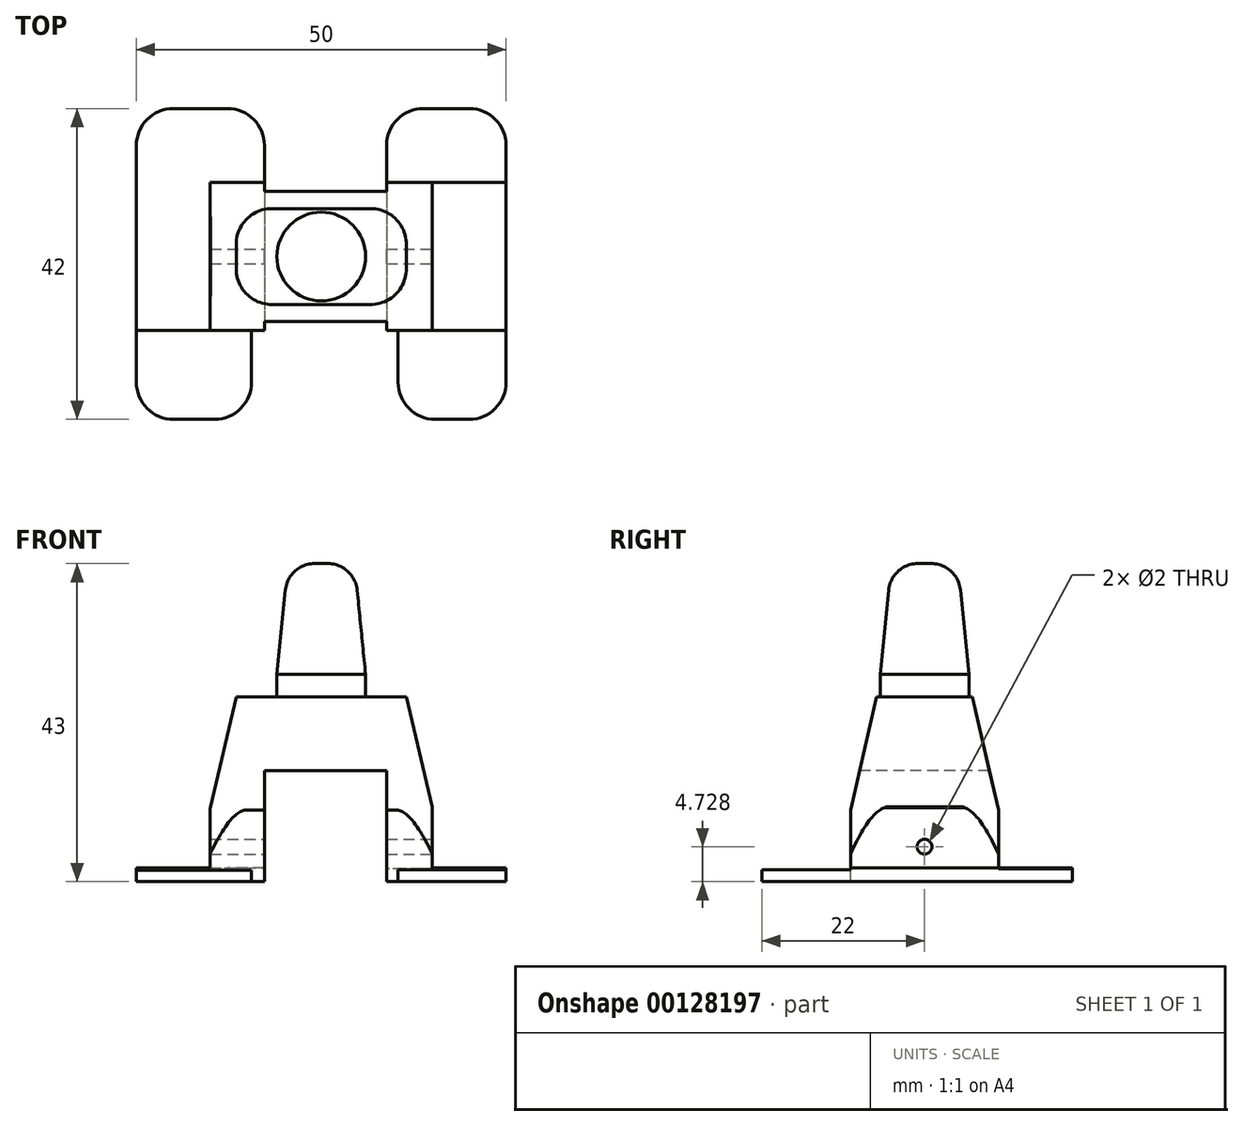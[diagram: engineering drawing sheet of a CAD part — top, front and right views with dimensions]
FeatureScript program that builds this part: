
annotation { "Feature Type Name" : "Feature", "Feature Type Description" : "" }
export const myFeature = defineFeature(function(context is Context, id is Id, definition is map)
    precondition{}
    {
        {
            var Q0;
            Q0=qCreatedBy(makeId("Front.planeOp"),FACE);
            var sketch = newSketch(context, id + "F0", { "sketchPlane" : qUnion([Q0])});
            skLineSegment(sketch, "E0.bottom", {"start": v(15, -12.5) * mm, "end": v(-15, -12.5) * mm});
            skLineSegment(sketch, "E0.top", {"start": v(15, 12.5) * mm, "end": v(-15, 12.5) * mm});
            skLineSegment(sketch, "E0.left", {"start": v(15, -12.5) * mm, "end": v(15, 12.5) * mm});
            skLineSegment(sketch, "E0.right", {"start": v(-15, -12.5) * mm, "end": v(-15, 12.5) * mm});
            skPoint(sketch, "E0.middle", {"position": v(0, 0) * mm});
            skSolve(sketch);
        }
        {
            var Q0;
            Q0=makeQuery(id+"F0.imprint","IMPRINT",FACE,{"disambiguationData":[TD([[makeQuery(id+"F0.imprint","IMPRINT",EDGE,{"derivedFrom":sQuery(id+"F0.wireOp",EDGE,"E0.bottom")}),-1.0]])]});
            extrude(context, id + "F1", {"entities" : qUnion([Q0]), "depth" : 20 * mm});
        }
        {
            var Q0;
            Q0=makeQuery(id+"F1.opExtrude","CAP_FACE",FACE,{"disambiguationData":[OSD([sQuery(id+"F0.wireOp",EDGE,"E0.bottom"),sQuery(id+"F0.wireOp",EDGE,"E0.top"),sQuery(id+"F0.wireOp",EDGE,"E0.left"),sQuery(id+"F0.wireOp",EDGE,"E0.right")])],"isStart":false});
            var sketch = newSketch(context, id + "F2", { "sketchPlane" : qUnion([Q0])});
            skLineSegment(sketch, "E1.bottom", {"start": v(-7.68, -12.5) * mm, "end": v(8.82, -12.5) * mm});
            skLineSegment(sketch, "E1.top", {"start": v(-7.68, 2.5) * mm, "end": v(8.82, 2.5) * mm});
            skLineSegment(sketch, "E1.left", {"start": v(-7.68, -12.5) * mm, "end": v(-7.68, 2.5) * mm});
            skLineSegment(sketch, "E1.right", {"start": v(8.82, -12.5) * mm, "end": v(8.82, 2.5) * mm});
            skSolve(sketch);
        }
        {
            var Q0;
            Q0=makeQuery(id+"F2.imprint","IMPRINT",FACE,{"disambiguationData":[TD([[makeQuery(id+"F2.imprint","IMPRINT",EDGE,{"derivedFrom":sQuery(id+"F2.wireOp",EDGE,"E1.bottom")}),-1.0]])]});
            extrude(context, id + "F3", {"entities" : qUnion([Q0]), "operationType" : NewBodyOperationType.REMOVE, "endBound" : BoundingType.THROUGH_ALL, "oppositeDirection" : true, "depth" : 25 * mm});
        }
        {
            var Q0;
            Q0=makeQuery(id+"F1.opExtrude","SWEPT_EDGE",EDGE,{"disambiguationData":[OSD([sQuery(id+"F0.wireOp",EDGE,"E0.top"),sQuery(id+"F0.wireOp",EDGE,"E0.left")])]});
            chamfer(context, id + "F4", {"entities" : qUnion([Q0]), "chamferType" : ChamferType.TWO_OFFSETS, "width1" : 2 * mm, "oppositeDirection" : false, "width2" : 15 * mm, "tangentPropagation" : true});
        }
        {
            var Q0;
            Q0=makeQuery(id+"F1.opExtrude","SWEPT_EDGE",EDGE,{"disambiguationData":[OSD([sQuery(id+"F0.wireOp",EDGE,"E0.top"),sQuery(id+"F0.wireOp",EDGE,"E0.right")])]});
            chamfer(context, id + "F5", {"entities" : qUnion([Q0]), "chamferType" : ChamferType.TWO_OFFSETS, "width1" : 15 * mm, "oppositeDirection" : false, "width2" : 2 * mm, "tangentPropagation" : true});
        }
        {
            var Q0;
            Q0=makeQuery(id+"F1.opExtrude","SWEPT_FACE",FACE,{"disambiguationData":[OSD([sQuery(id+"F0.wireOp",EDGE,"E0.top")])]});
            chamfer(context, id + "F6", {"entities" : qUnion([Q0]), "chamferType" : ChamferType.TWO_OFFSETS, "width1" : 1.5 * mm, "oppositeDirection" : false, "width2" : 15 * mm, "tangentPropagation" : true});
        }
        {
            var Q0;
            Q0=makeQuery(id+"F1.opExtrude","SWEPT_FACE",FACE,{"disambiguationData":[OSD([sQuery(id+"F0.wireOp",EDGE,"E0.top")])]});
            var sketch = newSketch(context, id + "F7", { "sketchPlane" : qUnion([Q0])});
            skCircle(sketch, "E2", {"center": v(0, -10) * mm, "radius": 6 * mm});
            skPoint(sketch, "E2.centerSnap0", {"position": v(-11.5, -10) * mm});
            skSolve(sketch);
        }
        {
            var Q0;
            {var subQ0=sQuery(id+"F7.wireOp",EDGE,"E2");var subQ1=sQuery(id+"F0.wireOp",EDGE,"E0.top");var subQ2=makeQuery(id+"F1.opExtrude","SWEPT_FACE",FACE,{"disambiguationData":[OSD([subQ1])]});var subQ3=makeQuery(id+"F6.opChamfer","BLEND_EDGE",EDGE,{"blendedFrom":[makeQuery(id+"F1.opExtrude","CAP_EDGE",EDGE,{"disambiguationData":[OSD([subQ1])],"isStart":true}),subQ2],"blendedInto":[subQ2]});var subQ4=makeQuery(id+"F7.imprint","INTERSECT",VERTEX,{"disambiguationData":[OD(0.0)],"derivedFrom":[subQ3,subQ0]});Q0=makeQuery(id+"F7.imprint","IMPRINT",FACE,{"disambiguationData":[TD([[makeQuery(id+"F7.imprint","IMPRINT",EDGE,{"disambiguationData":[TD([[subQ4,-1.0]])],"derivedFrom":subQ0}),1.0]])]});}
            extrude(context, id + "F8", {"entities" : qUnion([Q0]), "operationType" : NewBodyOperationType.ADD, "depth" : 18 * mm});
        }
        {
            var Q0;
            {var subQ0=sQuery(id+"F0.wireOp",EDGE,"E0.top");Q0=makeQuery(id+"F6.opChamfer","BLEND_EDGE",EDGE,{"blendedFrom":[makeQuery(id+"F4.opChamfer","BLEND_EDGE",EDGE,{"blendedFrom":[makeQuery(id+"F1.opExtrude","SWEPT_EDGE",EDGE,{"disambiguationData":[OSD([subQ0,sQuery(id+"F0.wireOp",EDGE,"E0.left")])]}),makeQuery(id+"F1.opExtrude","SWEPT_FACE",FACE,{"disambiguationData":[OSD([subQ0])]})],"blendedInto":[makeQuery(id+"F1.opExtrude","SWEPT_FACE",FACE,{"disambiguationData":[OSD([subQ0])]})]}),makeQuery(id+"F1.opExtrude","CAP_EDGE",EDGE,{"disambiguationData":[OSD([subQ0])],"isStart":false})],"blendedInto":[]});}
            var Q1;
            {var subQ0=sQuery(id+"F0.wireOp",EDGE,"E0.top");Q1=makeQuery(id+"F6.opChamfer","BLEND_EDGE",EDGE,{"blendedFrom":[makeQuery(id+"F4.opChamfer","BLEND_EDGE",EDGE,{"blendedFrom":[makeQuery(id+"F1.opExtrude","SWEPT_EDGE",EDGE,{"disambiguationData":[OSD([subQ0,sQuery(id+"F0.wireOp",EDGE,"E0.left")])]}),makeQuery(id+"F1.opExtrude","SWEPT_FACE",FACE,{"disambiguationData":[OSD([subQ0])]})],"blendedInto":[makeQuery(id+"F1.opExtrude","SWEPT_FACE",FACE,{"disambiguationData":[OSD([subQ0])]})]}),makeQuery(id+"F1.opExtrude","CAP_EDGE",EDGE,{"disambiguationData":[OSD([subQ0])],"isStart":true})],"blendedInto":[]});}
            var Q2;
            {var subQ0=sQuery(id+"F0.wireOp",EDGE,"E0.top");Q2=makeQuery(id+"F6.opChamfer","BLEND_EDGE",EDGE,{"blendedFrom":[makeQuery(id+"F5.opChamfer","BLEND_EDGE",EDGE,{"blendedFrom":[makeQuery(id+"F1.opExtrude","SWEPT_EDGE",EDGE,{"disambiguationData":[OSD([subQ0,sQuery(id+"F0.wireOp",EDGE,"E0.right")])]}),makeQuery(id+"F1.opExtrude","SWEPT_FACE",FACE,{"disambiguationData":[OSD([subQ0])]})],"blendedInto":[makeQuery(id+"F1.opExtrude","SWEPT_FACE",FACE,{"disambiguationData":[OSD([subQ0])]})]}),makeQuery(id+"F1.opExtrude","CAP_EDGE",EDGE,{"disambiguationData":[OSD([subQ0])],"isStart":false})],"blendedInto":[]});}
            var Q3;
            {var subQ0=sQuery(id+"F0.wireOp",EDGE,"E0.top");Q3=makeQuery(id+"F6.opChamfer","BLEND_EDGE",EDGE,{"blendedFrom":[makeQuery(id+"F5.opChamfer","BLEND_EDGE",EDGE,{"blendedFrom":[makeQuery(id+"F1.opExtrude","SWEPT_EDGE",EDGE,{"disambiguationData":[OSD([subQ0,sQuery(id+"F0.wireOp",EDGE,"E0.right")])]}),makeQuery(id+"F1.opExtrude","SWEPT_FACE",FACE,{"disambiguationData":[OSD([subQ0])]})],"blendedInto":[makeQuery(id+"F1.opExtrude","SWEPT_FACE",FACE,{"disambiguationData":[OSD([subQ0])]})]}),makeQuery(id+"F1.opExtrude","CAP_EDGE",EDGE,{"disambiguationData":[OSD([subQ0])],"isStart":true})],"blendedInto":[]});}
            fillet(context, id + "F9", {"entities" : qUnion([Q0, Q1, Q2, Q3]), "radius" : 5 * mm, "tangentPropagation" : true, "allowEdgeOverflow" : false});
        }
        {
            var Q0;
            Q0=makeQuery(id+"F1.opExtrude","SWEPT_FACE",FACE,{"disambiguationData":[OSD([sQuery(id+"F0.wireOp",EDGE,"E0.left")])]});
            var sketch = newSketch(context, id + "F10", { "sketchPlane" : qUnion([Q0])});
            skPoint(sketch, "E3", {"position": v(-10, -7.77) * mm});
            skPoint(sketch, "E3.positionSnap0", {"position": v(-10, -12.5) * mm});
            skSolve(sketch);
        }
        {
            var Q0;
            Q0=sQuery(id+"F10.wireOp",VERTEX,"E3");
            var Q1;
            Q1=makeQuery(id+"F1.opExtrude","SWEPT_BODY",BODY,{"disambiguationData":[OSD([sQuery(id+"F0.wireOp",EDGE,"E0.bottom"),sQuery(id+"F0.wireOp",EDGE,"E0.top"),sQuery(id+"F0.wireOp",EDGE,"E0.left"),sQuery(id+"F0.wireOp",EDGE,"E0.right")])]});
            hole(context, id + "F11", {"style" : HoleStyle.SIMPLE, "endStyle" : HoleEndStyle.THROUGH, "holeDiameter" : 2 * mm, "locations" : qUnion([Q0]), "scope" : qUnion([Q1]), "isTappedThrough" : true});
        }
        {
            var Q0;
            Q0=makeQuery(id+"F1.opExtrude","SWEPT_FACE",FACE,{"disambiguationData":[OSD([sQuery(id+"F0.wireOp",EDGE,"E0.left")])]});
            var sketch = newSketch(context, id + "F12", { "sketchPlane" : qUnion([Q0])});
            skLineSegment(sketch, "E4.bottom", {"start": v(-20, -12.5) * mm, "end": v(0, -12.5) * mm});
            skLineSegment(sketch, "E4.top", {"start": v(-20, -10.62) * mm, "end": v(0, -10.62) * mm});
            skLineSegment(sketch, "E4.left", {"start": v(-20, -12.5) * mm, "end": v(-20, -10.62) * mm});
            skLineSegment(sketch, "E4.right", {"start": v(0, -12.5) * mm, "end": v(0, -10.62) * mm});
            skSolve(sketch);
        }
        {
            var Q0;
            Q0=makeQuery(id+"F1.opExtrude","SWEPT_FACE",FACE,{"disambiguationData":[OSD([sQuery(id+"F0.wireOp",EDGE,"E0.right")])]});
            var sketch = newSketch(context, id + "F13", { "sketchPlane" : qUnion([Q0])});
            skLineSegment(sketch, "E5.bottom", {"start": v(0, -12.5) * mm, "end": v(20, -12.5) * mm});
            skLineSegment(sketch, "E5.top", {"start": v(0, -10.62) * mm, "end": v(20, -10.62) * mm});
            skLineSegment(sketch, "E5.left", {"start": v(0, -12.5) * mm, "end": v(0, -10.62) * mm});
            skLineSegment(sketch, "E5.right", {"start": v(20, -12.5) * mm, "end": v(20, -10.62) * mm});
            skSolve(sketch);
        }
        {
            var Q0;
            Q0=makeQuery(id+"F13.imprint","IMPRINT",FACE,{"disambiguationData":[TD([[makeQuery(id+"F13.imprint","IMPRINT",EDGE,{"derivedFrom":sQuery(id+"F13.wireOp",EDGE,"E5.bottom")}),-1.0]])]});
            extrude(context, id + "F14", {"entities" : qUnion([Q0]), "operationType" : NewBodyOperationType.ADD, "depth" : 10 * mm});
        }
        {
            var Q0;
            Q0=makeQuery(id+"F12.imprint","IMPRINT",FACE,{"disambiguationData":[TD([[makeQuery(id+"F12.imprint","IMPRINT",EDGE,{"derivedFrom":sQuery(id+"F12.wireOp",EDGE,"E4.bottom")}),1.0]])]});
            extrude(context, id + "F15", {"entities" : qUnion([Q0]), "operationType" : NewBodyOperationType.ADD, "depth" : 10 * mm});
        }
        {
            var Q0;
            Q0=makeQuery(id+"F14.boolean.opBoolean","MERGE",FACE,{"derivedFrom":[makeQuery(id+"F6.opChamfer","SPLIT",FACE,{"disambiguationData":[OD(1.0)],"derivedFrom":makeQuery(id+"F1.opExtrude","CAP_FACE",FACE,{"disambiguationData":[OSD([sQuery(id+"F0.wireOp",EDGE,"E0.bottom"),sQuery(id+"F0.wireOp",EDGE,"E0.top"),sQuery(id+"F0.wireOp",EDGE,"E0.left"),sQuery(id+"F0.wireOp",EDGE,"E0.right")])],"isStart":false})}),makeQuery(id+"F14.opExtrude","SWEPT_FACE",FACE,{"disambiguationData":[OSD([sQuery(id+"F13.wireOp",EDGE,"E5.right")])]})]});
            var sketch = newSketch(context, id + "F16", { "sketchPlane" : qUnion([Q0])});
            skLineSegment(sketch, "E6.bottom", {"start": v(-25, -12.5) * mm, "end": v(-9.42, -12.5) * mm});
            skLineSegment(sketch, "E6.top", {"start": v(-25, -10.98) * mm, "end": v(-9.42, -10.98) * mm});
            skLineSegment(sketch, "E6.left", {"start": v(-25, -12.5) * mm, "end": v(-25, -10.98) * mm});
            skLineSegment(sketch, "E6.right", {"start": v(-9.42, -12.5) * mm, "end": v(-9.42, -10.98) * mm});
            skSolve(sketch);
        }
        {
            var Q0;
            Q0=makeQuery(id+"F15.boolean.opBoolean","MERGE",FACE,{"derivedFrom":[makeQuery(id+"F6.opChamfer","SPLIT",FACE,{"disambiguationData":[OD(0.0)],"derivedFrom":makeQuery(id+"F1.opExtrude","CAP_FACE",FACE,{"disambiguationData":[OSD([sQuery(id+"F0.wireOp",EDGE,"E0.bottom"),sQuery(id+"F0.wireOp",EDGE,"E0.top"),sQuery(id+"F0.wireOp",EDGE,"E0.left"),sQuery(id+"F0.wireOp",EDGE,"E0.right")])],"isStart":false})}),makeQuery(id+"F15.opExtrude","SWEPT_FACE",FACE,{"disambiguationData":[OSD([sQuery(id+"F12.wireOp",EDGE,"E4.left")])]})]});
            var sketch = newSketch(context, id + "F17", { "sketchPlane" : qUnion([Q0])});
            skLineSegment(sketch, "E7.bottom", {"start": v(25, -12.5) * mm, "end": v(10.4, -12.5) * mm});
            skLineSegment(sketch, "E7.top", {"start": v(25, -10.87) * mm, "end": v(10.4, -10.87) * mm});
            skLineSegment(sketch, "E7.left", {"start": v(25, -12.5) * mm, "end": v(25, -10.87) * mm});
            skLineSegment(sketch, "E7.right", {"start": v(10.4, -12.5) * mm, "end": v(10.4, -10.87) * mm});
            skSolve(sketch);
        }
        {
            var Q0;
            Q0=makeQuery(id+"F16.imprint","IMPRINT",FACE,{"disambiguationData":[TD([[makeQuery(id+"F16.imprint","IMPRINT",EDGE,{"derivedFrom":sQuery(id+"F16.wireOp",EDGE,"E6.bottom")}),-1.0]])]});
            extrude(context, id + "F18", {"entities" : qUnion([Q0]), "operationType" : NewBodyOperationType.ADD, "depth" : 12 * mm});
        }
        {
            var Q0;
            Q0=makeQuery(id+"F17.imprint","IMPRINT",FACE,{"disambiguationData":[TD([[makeQuery(id+"F17.imprint","IMPRINT",EDGE,{"derivedFrom":sQuery(id+"F17.wireOp",EDGE,"E7.bottom")}),-1.0]])]});
            extrude(context, id + "F19", {"entities" : qUnion([Q0]), "operationType" : NewBodyOperationType.ADD, "depth" : 12 * mm});
        }
        {
            var Q0;
            Q0=makeQuery(id+"F15.boolean.opBoolean","MERGE",FACE,{"derivedFrom":[makeQuery(id+"F6.opChamfer","SPLIT",FACE,{"disambiguationData":[OD(0.0)],"derivedFrom":makeQuery(id+"F1.opExtrude","CAP_FACE",FACE,{"disambiguationData":[OSD([sQuery(id+"F0.wireOp",EDGE,"E0.bottom"),sQuery(id+"F0.wireOp",EDGE,"E0.top"),sQuery(id+"F0.wireOp",EDGE,"E0.left"),sQuery(id+"F0.wireOp",EDGE,"E0.right")])],"isStart":true})}),makeQuery(id+"F15.opExtrude","SWEPT_FACE",FACE,{"disambiguationData":[OSD([sQuery(id+"F12.wireOp",EDGE,"E4.right")])]})]});
            var sketch = newSketch(context, id + "F20", { "sketchPlane" : qUnion([Q0])});
            skLineSegment(sketch, "E8.bottom", {"start": v(-25, -12.5) * mm, "end": v(-8.82, -12.5) * mm});
            skLineSegment(sketch, "E8.top", {"start": v(-25, -10.76) * mm, "end": v(-8.82, -10.76) * mm});
            skLineSegment(sketch, "E8.left", {"start": v(-25, -12.5) * mm, "end": v(-25, -10.76) * mm});
            skLineSegment(sketch, "E8.right", {"start": v(-8.82, -12.5) * mm, "end": v(-8.82, -10.76) * mm});
            skSolve(sketch);
        }
        {
            var Q0;
            Q0=makeQuery(id+"F14.boolean.opBoolean","MERGE",FACE,{"derivedFrom":[makeQuery(id+"F6.opChamfer","SPLIT",FACE,{"disambiguationData":[OD(1.0)],"derivedFrom":makeQuery(id+"F1.opExtrude","CAP_FACE",FACE,{"disambiguationData":[OSD([sQuery(id+"F0.wireOp",EDGE,"E0.bottom"),sQuery(id+"F0.wireOp",EDGE,"E0.top"),sQuery(id+"F0.wireOp",EDGE,"E0.left"),sQuery(id+"F0.wireOp",EDGE,"E0.right")])],"isStart":true})}),makeQuery(id+"F14.opExtrude","SWEPT_FACE",FACE,{"disambiguationData":[OSD([sQuery(id+"F13.wireOp",EDGE,"E5.left")])]})]});
            var sketch = newSketch(context, id + "F21", { "sketchPlane" : qUnion([Q0])});
            skLineSegment(sketch, "E9.bottom", {"start": v(25, -12.5) * mm, "end": v(7.68, -12.5) * mm});
            skLineSegment(sketch, "E9.top", {"start": v(25, -10.62) * mm, "end": v(7.68, -10.62) * mm});
            skLineSegment(sketch, "E9.left", {"start": v(25, -12.5) * mm, "end": v(25, -10.62) * mm});
            skLineSegment(sketch, "E9.right", {"start": v(7.68, -12.5) * mm, "end": v(7.68, -10.62) * mm});
            skSolve(sketch);
        }
        {
            var Q0;
            Q0=makeQuery(id+"F20.imprint","IMPRINT",FACE,{"disambiguationData":[TD([[makeQuery(id+"F20.imprint","IMPRINT",EDGE,{"derivedFrom":sQuery(id+"F20.wireOp",EDGE,"E8.bottom")}),1.0]])]});
            extrude(context, id + "F22", {"entities" : qUnion([Q0]), "operationType" : NewBodyOperationType.ADD, "depth" : 10 * mm});
        }
        {
            var Q0;
            Q0=makeQuery(id+"F21.imprint","IMPRINT",FACE,{"disambiguationData":[TD([[makeQuery(id+"F21.imprint","IMPRINT",EDGE,{"derivedFrom":sQuery(id+"F21.wireOp",EDGE,"E9.bottom")}),1.0]])]});
            extrude(context, id + "F23", {"entities" : qUnion([Q0]), "operationType" : NewBodyOperationType.ADD, "depth" : 10 * mm});
        }
        {
            var Q0;
            Q0=makeQuery(id+"F19.opExtrude","CAP_EDGE",EDGE,{"disambiguationData":[OSD([sQuery(id+"F17.wireOp",EDGE,"E7.left")])],"isStart":false});
            var Q1;
            Q1=makeQuery(id+"F19.opExtrude","CAP_EDGE",EDGE,{"disambiguationData":[OSD([sQuery(id+"F17.wireOp",EDGE,"E7.right")])],"isStart":false});
            var Q2;
            Q2=makeQuery(id+"F18.opExtrude","CAP_EDGE",EDGE,{"disambiguationData":[OSD([sQuery(id+"F16.wireOp",EDGE,"E6.right")])],"isStart":false});
            var Q3;
            Q3=makeQuery(id+"F18.opExtrude","CAP_EDGE",EDGE,{"disambiguationData":[OSD([sQuery(id+"F16.wireOp",EDGE,"E6.left")])],"isStart":false});
            var Q4;
            Q4=makeQuery(id+"F23.opExtrude","CAP_EDGE",EDGE,{"disambiguationData":[OSD([sQuery(id+"F21.wireOp",EDGE,"E9.left")])],"isStart":false});
            var Q5;
            Q5=makeQuery(id+"F22.opExtrude","CAP_EDGE",EDGE,{"disambiguationData":[OSD([sQuery(id+"F20.wireOp",EDGE,"E8.left")])],"isStart":false});
            var Q6;
            Q6=makeQuery(id+"F22.opExtrude","CAP_EDGE",EDGE,{"disambiguationData":[OSD([sQuery(id+"F20.wireOp",EDGE,"E8.right")])],"isStart":false});
            var Q7;
            Q7=makeQuery(id+"F23.opExtrude","CAP_EDGE",EDGE,{"disambiguationData":[OSD([sQuery(id+"F21.wireOp",EDGE,"E9.right")])],"isStart":false});
            fillet(context, id + "F24", {"entities" : qUnion([Q0, Q1, Q2, Q3, Q4, Q5, Q6, Q7]), "radius" : 5 * mm, "tangentPropagation" : true, "allowEdgeOverflow" : false});
        }
        {
            var Q0;
            Q0=makeQuery(id+"F8.opExtrude","CAP_EDGE",EDGE,{"disambiguationData":[OSD([sQuery(id+"F7.wireOp",EDGE,"E2")])],"isStart":false});
            chamfer(context, id + "F25", {"entities" : qUnion([Q0]), "chamferType" : ChamferType.TWO_OFFSETS, "width1" : 1.5 * mm, "oppositeDirection" : false, "width2" : 15 * mm, "tangentPropagation" : true});
        }
        {
            var Q0;
            {var subQ0=sQuery(id+"F7.wireOp",EDGE,"E2");Q0=makeQuery(id+"F25.opChamfer","BLEND_EDGE",EDGE,{"blendedFrom":[makeQuery(id+"F8.opExtrude","CAP_EDGE",EDGE,{"disambiguationData":[OSD([subQ0])],"isStart":false}),makeQuery(id+"F8.opExtrude","CAP_FACE",FACE,{"disambiguationData":[OSD([subQ0])],"isStart":false})],"blendedInto":[makeQuery(id+"F8.opExtrude","CAP_FACE",FACE,{"disambiguationData":[OSD([subQ0])],"isStart":false})]});}
            fillet(context, id + "F26", {"entities" : qUnion([Q0]), "radius" : 4 * mm, "tangentPropagation" : true, "allowEdgeOverflow" : false});
        }
    });
